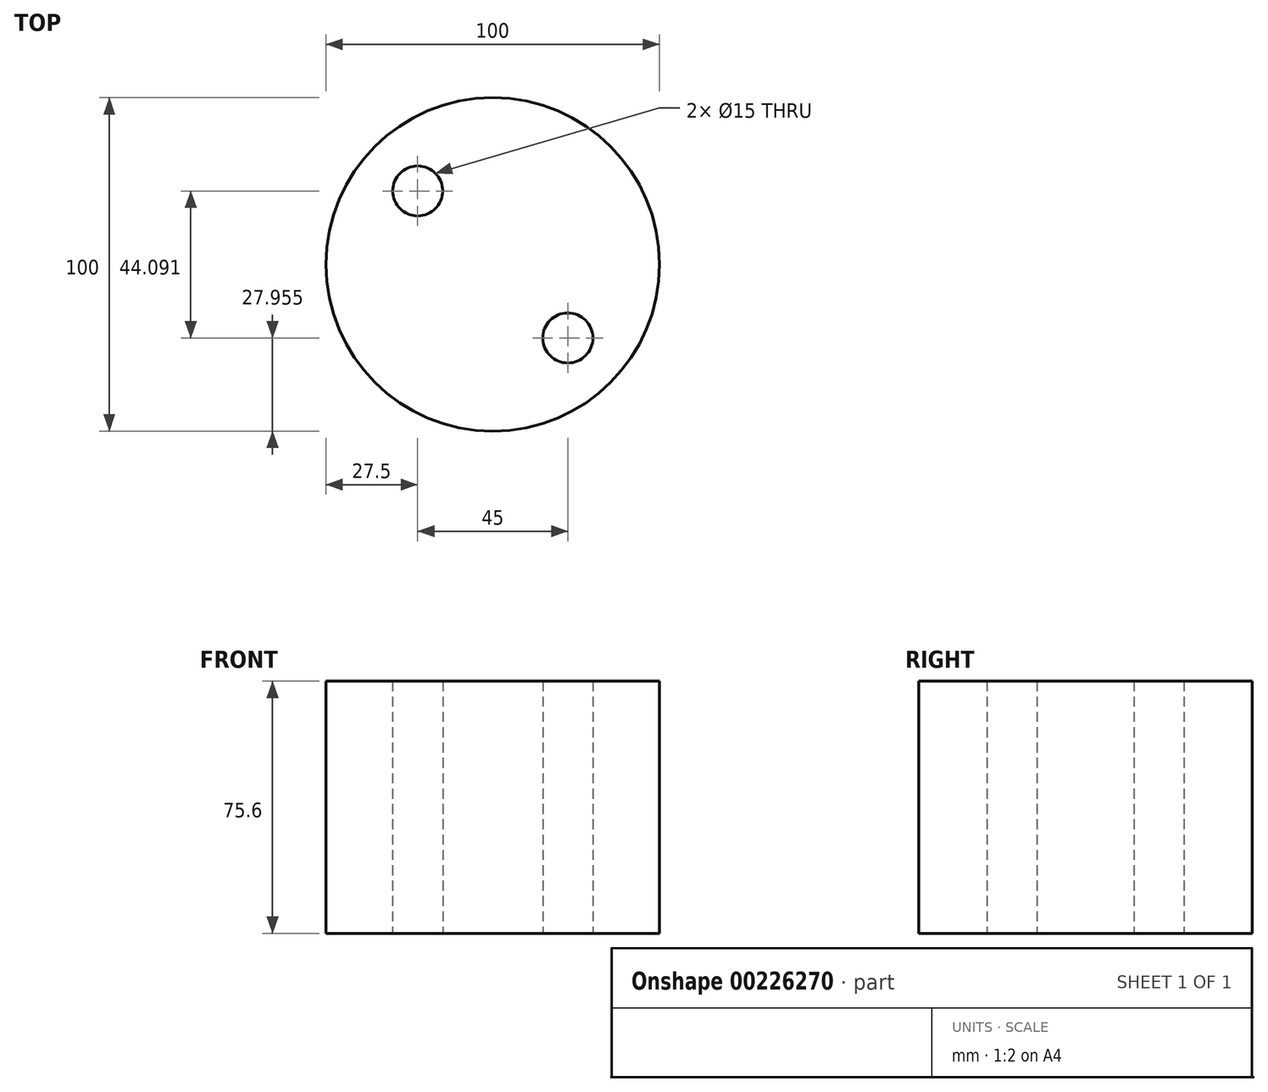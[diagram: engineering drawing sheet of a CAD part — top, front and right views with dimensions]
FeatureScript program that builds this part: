
annotation { "Feature Type Name" : "Feature", "Feature Type Description" : "" }
export const myFeature = defineFeature(function(context is Context, id is Id, definition is map)
    precondition{}
    {
        {
            var Q0;
            Q0=qCreatedBy(makeId("Top.planeOp"),FACE);
            var sketch = newSketch(context, id + "F0", { "sketchPlane" : qUnion([Q0])});
            skCircle(sketch, "E0", {"center": v(0, 0) * mm, "radius": 50 * mm});
            skCircle(sketch, "E1", {"center": v(-22.5, -22.05) * mm, "radius": 7.5 * mm});
            skCircle(sketch, "E2.MirrorC", {"center": v(22.5, -22.05) * mm, "radius": 7.5 * mm});
            skCircle(sketch, "E3.MirrorC", {"center": v(22.5, 22.05) * mm, "radius": 7.5 * mm});
            skCircle(sketch, "E4.MirrorC", {"center": v(-22.5, 22.05) * mm, "radius": 7.5 * mm});
            skSolve(sketch);
        }
        {
            var Q0;
            Q0=makeQuery(id+"F0.imprint","IMPRINT",FACE,{"disambiguationData":[TD([[makeQuery(id+"F0.imprint","IMPRINT",EDGE,{"derivedFrom":sQuery(id+"F0.wireOp",EDGE,"E2.MirrorC")}),-1.0]])]});
            var Q1;
            Q1=makeQuery(id+"F0.imprint","IMPRINT",FACE,{"disambiguationData":[TD([[makeQuery(id+"F0.imprint","IMPRINT",EDGE,{"derivedFrom":sQuery(id+"F0.wireOp",EDGE,"E1")}),1.0]])]});
            var Q2;
            Q2=makeQuery(id+"F0.imprint","IMPRINT",FACE,{"disambiguationData":[TD([[makeQuery(id+"F0.imprint","IMPRINT",EDGE,{"derivedFrom":sQuery(id+"F0.wireOp",EDGE,"E3.MirrorC")}),1.0]])]});
            var Q3;
            Q3=makeQuery(id+"F0.imprint","IMPRINT",FACE,{"disambiguationData":[TD([[makeQuery(id+"F0.imprint","IMPRINT",EDGE,{"derivedFrom":sQuery(id+"F0.wireOp",EDGE,"E0")}),1.0]])]});
            var Q4;
            Q4=makeQuery(id+"F0.imprint","IMPRINT",FACE,{"disambiguationData":[TD([[makeQuery(id+"F0.imprint","IMPRINT",EDGE,{"derivedFrom":sQuery(id+"F0.wireOp",EDGE,"E4.MirrorC")}),-1.0]])]});
            extrude(context, id + "F1", {"entities" : qUnion([Q0, Q1, Q2, Q3, Q4]), "depth" : 20 * mm});
        }
        {
            var Q0;
            Q0=makeQuery(id+"F0.imprint","IMPRINT",FACE,{"disambiguationData":[TD([[makeQuery(id+"F0.imprint","IMPRINT",EDGE,{"derivedFrom":sQuery(id+"F0.wireOp",EDGE,"E3.MirrorC")}),1.0]])]});
            var Q1;
            Q1=makeQuery(id+"F0.imprint","IMPRINT",FACE,{"disambiguationData":[TD([[makeQuery(id+"F0.imprint","IMPRINT",EDGE,{"derivedFrom":sQuery(id+"F0.wireOp",EDGE,"E4.MirrorC")}),-1.0]])]});
            var Q2;
            Q2=makeQuery(id+"F0.imprint","IMPRINT",FACE,{"disambiguationData":[TD([[makeQuery(id+"F0.imprint","IMPRINT",EDGE,{"derivedFrom":sQuery(id+"F0.wireOp",EDGE,"E1")}),1.0]])]});
            var Q3;
            Q3=makeQuery(id+"F0.imprint","IMPRINT",FACE,{"disambiguationData":[TD([[makeQuery(id+"F0.imprint","IMPRINT",EDGE,{"derivedFrom":sQuery(id+"F0.wireOp",EDGE,"E2.MirrorC")}),-1.0]])]});
            extrude(context, id + "F2", {"entities" : qUnion([Q0, Q1, Q2, Q3]), "operationType" : NewBodyOperationType.ADD, "oppositeDirection" : true, "depth" : 55.6 * mm});
        }
    });
